# Revit family: Plumbing-Flushometer-Sloan-Valve-BPW-1010
name_source: partatom
category: Plumbing Fixtures
units: mm (PartAtom-declared; Revit-internal decimal feet)

## family parameters
Cut with Voids When Loaded = No
Host = Face
OmniClass Number = 23.45.05.14.99
Part Type = Normal
Room Calculation Point = No
Round Connector Dimension = Use Diameter
Shared = No

## types (4) — shared parameters
Assembly Code = D2020300
CW Connection = Yes
Centerline of Supply from Top of Fixture = 34 1/2"
Centerline of Supply to Centerline of Valve = 5"
Default Elevation = 0"
Edition number = 1
HW Connection = No
Height = 36 1/2"
Keynote = 15410
Manufacturer = Sloan Valve
Operating Water Pressure = 15 – 80 PSI (103 – 552 kPa)
Product Material = Sloan Valve - Finish - Polished Chrome
URL = www.sloanvalve.com
Valve Pressure Drop = 0.00 psi
Vent Connection = No
Waste Connection = No
Water Inlet Connection Description = Water Inlet Connection
Water Inlet Connection Diameter = 1"
z_2D_1 = Yes
z_Distance = 2 1/2"
z_Offset Group 1 = 0"
zero-valued in all types: CWFU, HWFU, WFU

## per-type parameters (varying)
| type | Description | Flush Rate | Part Number | z_2D_1 1/2 | z_No OFST | z_OFST | z_Offset | z_Pipe Offset | z_cut offset |
| ROYAL BPW 1010-1.6 | 1.6 gpf, Polished Chrome Finish, Fixture Connection Top Spud, Single Flush, Royal® Exposed Manual Specialty Water Closet Bedpan Washer Flushometer. | 1.6 gpf (6.0 Lpf) | 3019618 | No | Yes | No | 2 1/2" | 1" | 3 1/2" |
| ROYAL BPW 1010-3.5 | 3.5 gpf, Polished Chrome Finish, Fixture Connection Top Spud, Single Flush, Royal® Exposed Manual Specialty Water Closet Bedpan Washer Flushometer. | 3.5 gpf (13.2 Lpf) | 3019600 | No | Yes | No | 2 1/2" | 1" | 3 1/2" |
| ROYAL BPW 1010-1.28 | 1.28 gpf, Polished Chrome Finish, Fixture Connection Top Spud, Single Flush, Royal® Exposed Manual Specialty Water Closet Bedpan Washer Flushometer. | 1.28 gpf (4.8 Lpf) | 3019661 | No | Yes | No | 2 1/2" | 1" | 3 1/2" |
| ROYAL BPW 1010-1.6-1-1/2-OFST | 1.6 gpf, Polished Chrome Finish, Fixture Connection Top Spud, Single Flush, 1.5 Offset, F182 Outlet Tube, Royal® Exposed Manual Specialty Water Closet Bedpan Washer Flushometer. | 1.6 gpf (6.0 Lpf) | 3019641 | Yes | No | Yes | 4" | 1 1/2" | 5" |

note: column(s) folded — value = type name in every type: Model

## geometry (parser evidence)
native form markers: Sweep x2
no freeform markers — native parametric forms only
